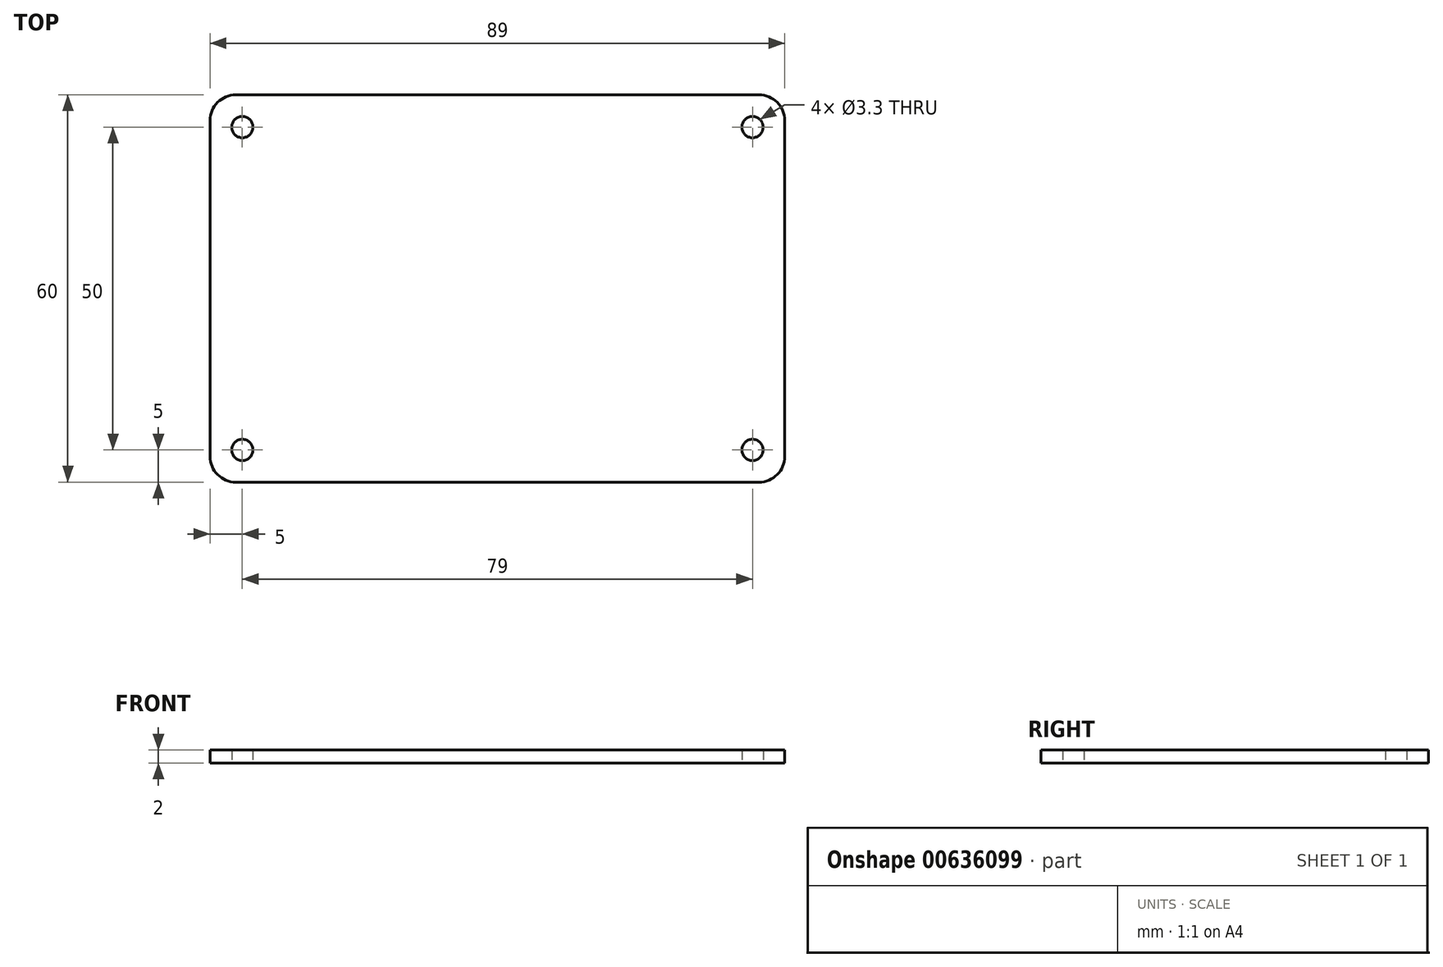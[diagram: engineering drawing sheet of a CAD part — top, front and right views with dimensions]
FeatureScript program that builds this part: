
annotation { "Feature Type Name" : "Feature", "Feature Type Description" : "" }
export const myFeature = defineFeature(function(context is Context, id is Id, definition is map)
    precondition{}
    {
        {
            var Q0;
            Q0=qCreatedBy(makeId("Top.planeOp"),FACE);
            var sketch = newSketch(context, id + "F0", { "sketchPlane" : qUnion([Q0])});
            skLineSegment(sketch, "E0.bottom", {"start": v(42.5, -28) * mm, "end": v(-42.5, -28) * mm});
            skLineSegment(sketch, "E0.top", {"start": v(42.5, 28) * mm, "end": v(-42.5, 28) * mm});
            skLineSegment(sketch, "E0.left", {"start": v(42.5, -28) * mm, "end": v(42.5, 28) * mm});
            skLineSegment(sketch, "E0.right", {"start": v(-42.5, -28) * mm, "end": v(-42.5, 28) * mm});
            skPoint(sketch, "E0.middle", {"position": v(0, 0) * mm});
            skCircle(sketch, "E1", {"center": v(-39.5, 25) * mm, "radius": 1.65 * mm});
            skCircle(sketch, "E2.MirrorC", {"center": v(39.5, 25) * mm, "radius": 1.65 * mm});
            skCircle(sketch, "E3.MirrorC", {"center": v(-39.5, -25) * mm, "radius": 1.65 * mm});
            skCircle(sketch, "E4.MirrorC", {"center": v(39.5, -25) * mm, "radius": 1.65 * mm});
            skSolve(sketch);
        }
        {
            var Q0;
            Q0 = qSketchRegion(id + "F0", true);
            extrude(context, id + "F1", {"entities" : qUnion([Q0]), "depth" : 2 * mm, "offsetDistance" : 25 * mm});
        }
        {
            var Q0;
            Q0=makeQuery(id+"F1.opExtrude","SWEPT_EDGE",EDGE,{"disambiguationData":[OSD([sQuery(id+"F0.wireOp",EDGE,"E0.bottom"),sQuery(id+"F0.wireOp",EDGE,"E0.right")])]});
            var Q1;
            Q1=makeQuery(id+"F1.opExtrude","SWEPT_EDGE",EDGE,{"disambiguationData":[OSD([sQuery(id+"F0.wireOp",EDGE,"E0.top"),sQuery(id+"F0.wireOp",EDGE,"E0.right")])]});
            var Q2;
            Q2=makeQuery(id+"F1.opExtrude","SWEPT_EDGE",EDGE,{"disambiguationData":[OSD([sQuery(id+"F0.wireOp",EDGE,"E0.bottom"),sQuery(id+"F0.wireOp",EDGE,"E0.left")])]});
            var Q3;
            Q3=makeQuery(id+"F1.opExtrude","SWEPT_EDGE",EDGE,{"disambiguationData":[OSD([sQuery(id+"F0.wireOp",EDGE,"E0.top"),sQuery(id+"F0.wireOp",EDGE,"E0.left")])]});
            fillet(context, id + "F2", {"entities" : qUnion([Q0, Q1, Q2, Q3]), "radius" : 2 * mm, "tangentPropagation" : true, "allowEdgeOverflow" : false});
        }
        {
            var Q0;
            Q0=makeQuery(id+"F1.opExtrude","CAP_FACE",FACE,{"disambiguationData":[OSD([sQuery(id+"F0.wireOp",EDGE,"E0.bottom"),sQuery(id+"F0.wireOp",EDGE,"E0.top"),sQuery(id+"F0.wireOp",EDGE,"E0.left"),sQuery(id+"F0.wireOp",EDGE,"E0.right"),sQuery(id+"F0.wireOp",EDGE,"E1"),sQuery(id+"F0.wireOp",EDGE,"E2.MirrorC"),sQuery(id+"F0.wireOp",EDGE,"E3.MirrorC"),sQuery(id+"F0.wireOp",EDGE,"E4.MirrorC")])],"isStart":false});
            var sketch = newSketch(context, id + "F3", { "sketchPlane" : qUnion([Q0])});
            skArc(sketch, "E5.0", {"start": v(44.5, 26) * mm, "mid": v(43.33, 28.83) * mm, "end": v(40.5, 30) * mm});
            skLineSegment(sketch, "E5.1", {"start": v(44.5, -26) * mm, "end": v(44.5, 26) * mm});
            skLineSegment(sketch, "E5.2", {"start": v(40.5, 30) * mm, "end": v(-40.5, 30) * mm});
            skArc(sketch, "E5.3", {"start": v(40.5, -30) * mm, "mid": v(43.33, -28.83) * mm, "end": v(44.5, -26) * mm});
            skArc(sketch, "E5.4", {"start": v(-40.5, 30) * mm, "mid": v(-43.33, 28.83) * mm, "end": v(-44.5, 26) * mm});
            skLineSegment(sketch, "E5.5", {"start": v(-44.5, -26) * mm, "end": v(-44.5, 26) * mm});
            skArc(sketch, "E5.6", {"start": v(-44.5, -26) * mm, "mid": v(-43.33, -28.83) * mm, "end": v(-40.5, -30) * mm});
            skLineSegment(sketch, "E5.7", {"start": v(40.5, -30) * mm, "end": v(-40.5, -30) * mm});
            skSolve(sketch);
        }
        {
            var Q0;
            Q0=makeQuery(id+"F3.imprint","IMPRINT",FACE,{"disambiguationData":[TD([[makeQuery(id+"F3.imprint","IMPRINT",EDGE,{"derivedFrom":sQuery(id+"F3.wireOp",EDGE,"E5.0")}),1.0]])]});
            var Q1;
            Q1=makeQuery(id+"F1.opExtrude","CAP_FACE",FACE,{"disambiguationData":[OSD([sQuery(id+"F0.wireOp",EDGE,"E0.bottom"),sQuery(id+"F0.wireOp",EDGE,"E0.top"),sQuery(id+"F0.wireOp",EDGE,"E0.left"),sQuery(id+"F0.wireOp",EDGE,"E0.right"),sQuery(id+"F0.wireOp",EDGE,"E1"),sQuery(id+"F0.wireOp",EDGE,"E2.MirrorC"),sQuery(id+"F0.wireOp",EDGE,"E3.MirrorC"),sQuery(id+"F0.wireOp",EDGE,"E4.MirrorC")])],"isStart":true});
            extrude(context, id + "F4", {"entities" : qUnion([Q0]), "operationType" : NewBodyOperationType.ADD, "endBound" : BoundingType.UP_TO_SURFACE, "oppositeDirection" : true, "depth" : 25 * mm, "endBoundEntityFace" : qUnion([Q1]), "offsetDistance" : 25 * mm});
        }
    });
